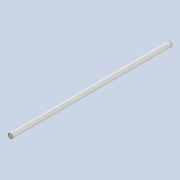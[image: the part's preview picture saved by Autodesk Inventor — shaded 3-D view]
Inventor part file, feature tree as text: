
AUTODESK INVENTOR PART (.ipt)
format: ipt  version: 2020 (Build 240168000, 168)  size: 73,728 bytes
history: native  units: mm
features: extrude x1, sketch x1
ambient origin geometry x8: Origin, YZ Plane, XZ Plane, XY Plane, X Axis, Y Axis, Z Axis, Center Point
bodies: Solid1 (feature_tree)
feature tree (2):
  extrude  "Extrusion1"  Depth=265.0mm TaperAngle=0.0deg
  sketch  "Sketch1"  dims[d0=8.0mm d1=265.0mm d2=0.0mm]
